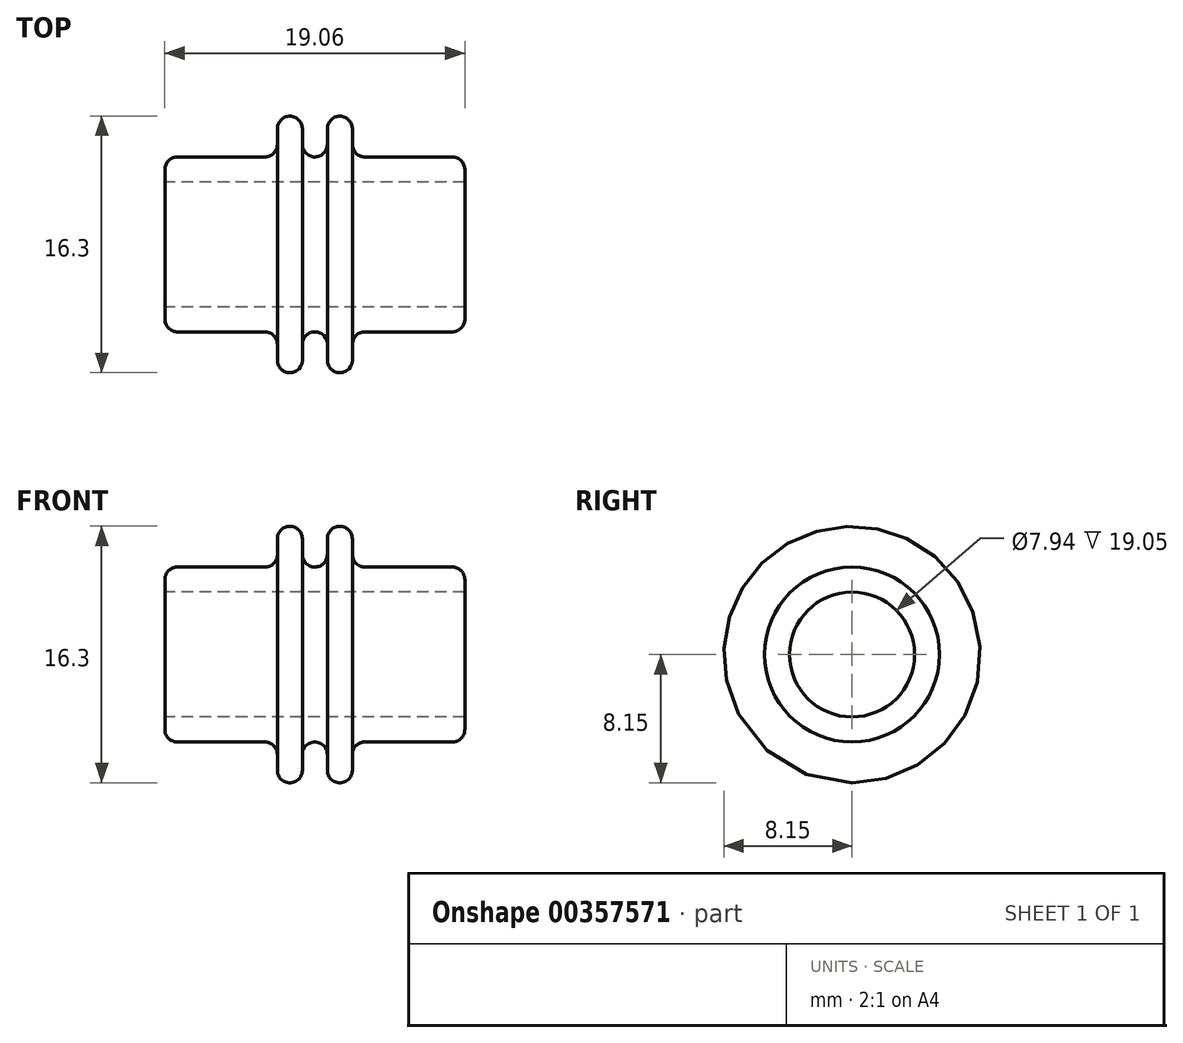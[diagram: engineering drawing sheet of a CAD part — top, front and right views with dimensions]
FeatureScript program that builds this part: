
annotation { "Feature Type Name" : "Feature", "Feature Type Description" : "" }
export const myFeature = defineFeature(function(context is Context, id is Id, definition is map)
    precondition{}
    {
        {
            var Q0;
            Q0=qCreatedBy(makeId("Front.planeOp"),FACE);
            var sketch = newSketch(context, id + "F0", { "sketchPlane" : qUnion([Q0])});
            skLineSegment(sketch, "E0", {"start": v(0, 3.97) * mm, "end": v(0, 5.56) * mm});
            skLineSegment(sketch, "E1", {"start": v(0, 5.56) * mm, "end": v(0.8, 5.56) * mm});
            skLineSegment(sketch, "E2", {"start": v(0.8, 5.56) * mm, "end": v(0.8, 8.15) * mm});
            skLineSegment(sketch, "E3", {"start": v(0.8, 8.15) * mm, "end": v(2.38, 8.15) * mm});
            skLineSegment(sketch, "E4", {"start": v(2.38, 8.15) * mm, "end": v(2.38, 5.56) * mm});
            skLineSegment(sketch, "E5", {"start": v(2.38, 5.56) * mm, "end": v(9.53, 5.56) * mm});
            skLineSegment(sketch, "E6", {"start": v(9.53, 5.56) * mm, "end": v(9.53, 3.97) * mm});
            skLineSegment(sketch, "E7", {"start": v(9.53, 3.97) * mm, "end": v(0, 3.97) * mm});
            skSolve(sketch);
        }
        {
            var Q0;
            Q0=qCreatedBy(makeId("Front.planeOp"),FACE);
            var sketch = newSketch(context, id + "F1", { "sketchPlane" : qUnion([Q0])});
            skLineSegment(sketch, "E8", {"start": v(0, 0) * mm, "end": v(2.02, 0) * mm, "construction": true});
            skSolve(sketch);
        }
        {
            var Q0;
            Q0=makeQuery(id+"F0.imprint","IMPRINT",FACE,{"disambiguationData":[TD([[makeQuery(id+"F0.imprint","IMPRINT",EDGE,{"derivedFrom":sQuery(id+"F0.wireOp",EDGE,"E0")}),-1.0]])]});
            var Q1;
            Q1=sQuery(id+"F1.wireOp",EDGE,"E8");
            revolve(context, id + "F2", {"entities" : qUnion([Q0]), "axis" : qUnion([Q1]), "revolveType" : RevolveType.FULL});
        }
        {
            var Q0;
            Q0=makeQuery(id+"F2.opRevolve","SWEPT_BODY",BODY,{"disambiguationData":[OSD([sQuery(id+"F0.wireOp",EDGE,"E0"),sQuery(id+"F0.wireOp",EDGE,"E1"),sQuery(id+"F0.wireOp",EDGE,"E2"),sQuery(id+"F0.wireOp",EDGE,"E3"),sQuery(id+"F0.wireOp",EDGE,"E4"),sQuery(id+"F0.wireOp",EDGE,"E5"),sQuery(id+"F0.wireOp",EDGE,"E6"),sQuery(id+"F0.wireOp",EDGE,"E7")])]});
            var Q1;
            Q1=makeQuery(id+"F2.opRevolve","SWEPT_FACE",FACE,{"disambiguationData":[OSD([sQuery(id+"F0.wireOp",EDGE,"E0")])]});
            mirror(context, id + "F3", {"operationType" : NewBodyOperationType.ADD, "entities" : qUnion([Q0]), "mirrorPlane" : qUnion([Q1])});
        }
        {
            var Q0;
            Q0=makeQuery(id+"F3.opPattern","COPY",EDGE,{"derivedFrom":makeQuery(id+"F2.opRevolve","SWEPT_EDGE",EDGE,{"disambiguationData":[OSD([sQuery(id+"F0.wireOp",EDGE,"E2"),sQuery(id+"F0.wireOp",EDGE,"E3")])]}),"instanceName":"1"});
            var Q1;
            Q1=makeQuery(id+"F3.opPattern","COPY",EDGE,{"derivedFrom":makeQuery(id+"F2.opRevolve","SWEPT_EDGE",EDGE,{"disambiguationData":[OSD([sQuery(id+"F0.wireOp",EDGE,"E3"),sQuery(id+"F0.wireOp",EDGE,"E4")])]}),"instanceName":"1"});
            var Q2;
            Q2=makeQuery(id+"F3.opPattern","COPY",EDGE,{"derivedFrom":makeQuery(id+"F2.opRevolve","SWEPT_EDGE",EDGE,{"disambiguationData":[OSD([sQuery(id+"F0.wireOp",EDGE,"E5"),sQuery(id+"F0.wireOp",EDGE,"E6")])]}),"instanceName":"1"});
            var Q3;
            Q3=makeQuery(id+"F3.opPattern","COPY",EDGE,{"derivedFrom":makeQuery(id+"F2.opRevolve","SWEPT_EDGE",EDGE,{"disambiguationData":[OSD([sQuery(id+"F0.wireOp",EDGE,"E4"),sQuery(id+"F0.wireOp",EDGE,"E5")])]}),"instanceName":"1"});
            var Q4;
            Q4=makeQuery(id+"F3.opPattern","COPY",EDGE,{"derivedFrom":makeQuery(id+"F2.opRevolve","SWEPT_EDGE",EDGE,{"disambiguationData":[OSD([sQuery(id+"F0.wireOp",EDGE,"E1"),sQuery(id+"F0.wireOp",EDGE,"E2")])]}),"instanceName":"1"});
            var Q5;
            Q5=makeQuery(id+"F2.opRevolve","SWEPT_EDGE",EDGE,{"disambiguationData":[OSD([sQuery(id+"F0.wireOp",EDGE,"E3"),sQuery(id+"F0.wireOp",EDGE,"E4")])]});
            var Q6;
            Q6=makeQuery(id+"F2.opRevolve","SWEPT_EDGE",EDGE,{"disambiguationData":[OSD([sQuery(id+"F0.wireOp",EDGE,"E2"),sQuery(id+"F0.wireOp",EDGE,"E3")])]});
            var Q7;
            Q7=makeQuery(id+"F2.opRevolve","SWEPT_EDGE",EDGE,{"disambiguationData":[OSD([sQuery(id+"F0.wireOp",EDGE,"E1"),sQuery(id+"F0.wireOp",EDGE,"E2")])]});
            var Q8;
            Q8=makeQuery(id+"F2.opRevolve","SWEPT_EDGE",EDGE,{"disambiguationData":[OSD([sQuery(id+"F0.wireOp",EDGE,"E4"),sQuery(id+"F0.wireOp",EDGE,"E5")])]});
            var Q9;
            Q9=makeQuery(id+"F2.opRevolve","SWEPT_EDGE",EDGE,{"disambiguationData":[OSD([sQuery(id+"F0.wireOp",EDGE,"E5"),sQuery(id+"F0.wireOp",EDGE,"E6")])]});
            fillet(context, id + "F4", {"entities" : qUnion([Q0, Q1, Q2, Q3, Q4, Q5, Q6, Q7, Q8, Q9]), "radius" : 0.8 * mm, "tangentPropagation" : true, "allowEdgeOverflow" : false});
        }
    });
